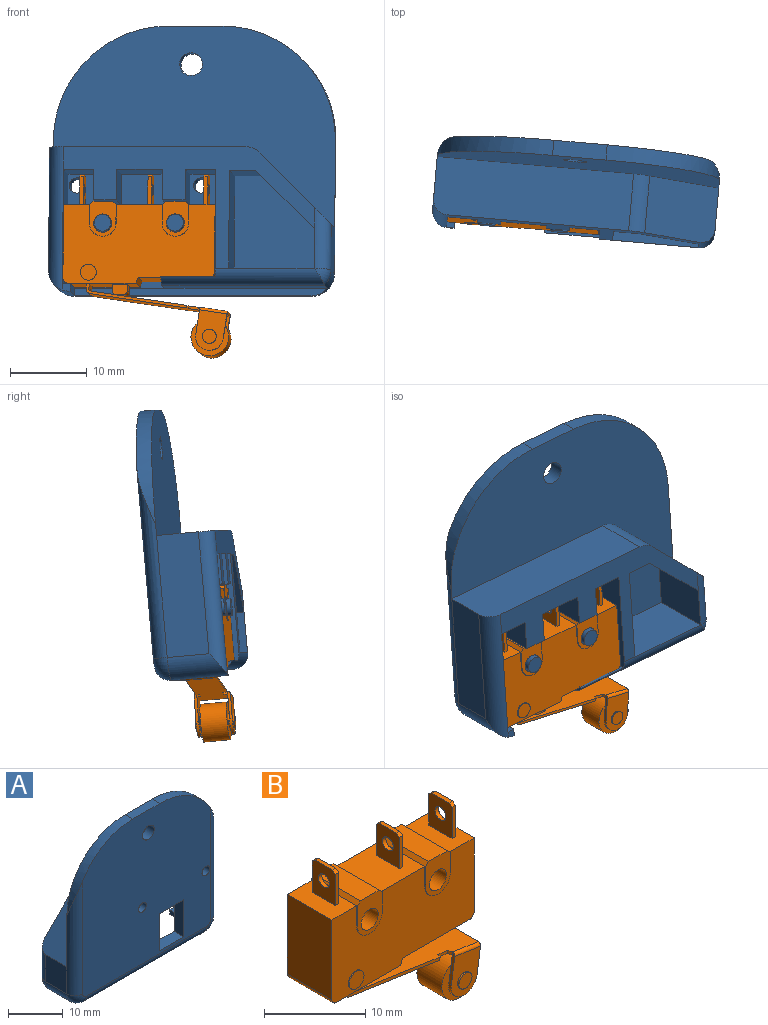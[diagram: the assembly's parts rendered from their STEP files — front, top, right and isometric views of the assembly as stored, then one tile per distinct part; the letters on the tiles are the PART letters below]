
ASSEMBLY  parts=2 mates=1
PART A: 60 faces, bbox 37x9.5x35.5 mm
  f0: plane 20x15mm, normal (0,1,0), area 203.7mm2, adj f4,f7,f8,f13,f14,f15,f16,f18
  f1: plane 33.46x33mm, normal (0,-1,0), area 982.1mm2, adj f29,f30,f31,f32,f36,f37,f40,f41
  f2: plane 33x16mm, normal (0,1,0), area 145mm2, adj f7,f8,f10,f11,f12,f13,f14,f20
  f3: plane 6x5.5mm, normal (-1,0,0), area 33mm2, adj f11,f39,f43,f46
  f4: plane 12.87x7mm, normal (0,0,1), area 12.9mm2, adj f0,f5,f15,f26,f27,f34
  f5: plane 1x1mm, normal (0,1,0), area 0.9mm2, adj f4,f27,f38,f48
  f6: plane 31x1mm, normal (0,0,-1), area 31mm2, adj f26,f38,f39,f42
  f7: plane 7x6mm, normal (0,0,-1), area 42mm2, adj f0,f2,f20,f23
  f8: plane 7x4mm, normal (0,0,-1), area 28mm2, adj f0,f2,f15,f24
  f9: plane 16x5.5mm, normal (1,0,0), area 88mm2, adj f10,f38,f40,f48
  f10: plane 25.76x7.5mm, normal (0,0,1), area 192.3mm2, adj f2,f9,f12,f28,f48
  f11: plane 9.12x9.12mm, normal (-0.71,0,0.71), area 95.5mm2, adj f2,f3,f12,f28,f46
  f12: cylinder r=3mm len=7.5mm, axis (0,1,0), area 17.7mm2, adj f2,f10,f11,f28
  f13: plane 14.01x7mm, normal (1,0,0), area 98mm2, adj f0,f2,f14,f33,f45
  f14: plane 7x4mm, normal (0,0,-1), area 28mm2, adj f0,f2,f13,f21
  f15: plane 15x7mm, normal (-1,0,0), area 105mm2, adj f0,f4,f8,f48
  f16: cylinder r=1.1mm len=7mm, axis (0,-1,0), area 48.4mm2, adj f0,f17
  f17: plane 2.2x2.2mm, normal (0,1,0), area 3.8mm2, adj f16
  f18: cylinder r=1.1mm len=7mm, axis (0,-1,0), area 48.4mm2, adj f0,f19
  f19: plane 2.2x2.2mm, normal (0,1,0), area 3.8mm2, adj f18
  f20: plane 7x4mm, normal (1,0,0), area 28mm2, adj f0,f2,f7,f22
  f21: plane 7x4mm, normal (-1,0,0), area 28mm2, adj f0,f2,f14,f22
  f22: plane 7x3mm, normal (0,0,-1), area 21mm2, adj f0,f2,f20,f21
  f23: plane 7x4mm, normal (-1,0,0), area 28mm2, adj f0,f2,f7,f25
  f24: plane 7x4mm, normal (1,0,0), area 28mm2, adj f0,f2,f8,f25
  f25: plane 7x3mm, normal (0,0,-1), area 21mm2, adj f0,f2,f23,f24
  f26: plane 33.24x1mm, normal (0,1,0), area 32.5mm2, adj f4,f6,f27,f35,f39
  f27: plane 6.5x1mm, normal (-1,0,0), area 6.5mm2, adj f4,f5,f26,f38
  f28: plane 37x26.46mm, normal (0,1,0), area 555.4mm2, adj f10,f11,f12,f29,f30,f36,f37,f40
  f29: plane 7x2mm, normal (0,0,1), area 14mm2, adj f1,f28,f36,f37
  f30: cylinder r=1.5mm len=3mm, axis (0,1,0), area 18.8mm2, adj f1,f28
  f31: cylinder r=1mm len=2.5mm, axis (0,1,0), area 15.7mm2, adj f0,f1
  f32: cylinder r=1mm len=2.5mm, axis (0,1,0), area 15.7mm2, adj f0,f1
  f33: plane 7.13x6.72mm, normal (0,0,1), area 47.9mm2, adj f0,f13,f34,f45
  f34: plane 6.72x0.99mm, normal (1,0,0), area 6.1mm2, adj f0,f4,f33,f35,f45
  f35: plane 21.37x4.5mm, normal (0,0,-1), area 96.1mm2, adj f26,f34,f39,f45
  f36: cylinder r=15mm len=15mm, axis (0,1,0), area 41mm2, adj f1,f28,f29,f43
  f37: cylinder r=15mm len=15mm, axis (0,-1,0), area 41mm2, adj f1,f28,f29,f40
  f38: cylinder r=3mm len=7.5mm, axis (0,-1,0), area 32.6mm2, adj f5,f6,f9,f27,f41,f48
  f39: cylinder r=3mm len=5.5mm, axis (0,1,0), area 14.6mm2, adj f3,f6,f26,f35,f44,f47
  f40: cylinder r=2mm len=24.94mm, axis (0,0,-1), area 67.4mm2, adj f1,f9,f28,f37,f41
  f41: torus R=1mm, axis (0,-1,0), area 11.2mm2, adj f1,f38,f40,f42
  f42: cylinder r=2mm len=31mm, axis (-1,0,0), area 97.4mm2, adj f1,f6,f41,f44
  f43: cylinder r=2mm len=24.94mm, axis (0,0,1), area 67.4mm2, adj f1,f3,f28,f36,f44
  f44: torus R=1mm, axis (0,-1,0), area 11.2mm2, adj f1,f39,f42,f43
  f45: cylinder r=2mm len=21.37mm, axis (-1,0,0), area 58.3mm2, adj f2,f13,f33,f34,f35,f47,f57
  f46: cylinder r=2mm len=8mm, axis (0,0,-1), area 21.1mm2, adj f2,f3,f11,f47,f58
  f47: torus R=1mm, axis (0,-1,0), area 4.3mm2, adj f39,f45,f46
  f48: cylinder r=2mm len=18.83mm, axis (0,0,1), area 55.5mm2, adj f2,f5,f9,f10,f15,f38
  f49: plane 6.22x2.5mm, normal (0,0,1), area 15.6mm2, adj f0,f1,f50,f52
  f50: plane 8.25x2.5mm, normal (1,0,0), area 20.6mm2, adj f0,f1,f49,f51
  f51: plane 6.22x2.5mm, normal (0,0,-1), area 15.6mm2, adj f0,f1,f50,f52
  f52: plane 8.25x2.5mm, normal (-1,0,0), area 20.6mm2, adj f0,f1,f49,f51
  f53: plane 8x7.79mm, normal (0.7,0,-0.72), area 87mm2, adj f2,f54,f58,f59
  f54: plane 8x3.43mm, normal (0,0,-1), area 27.4mm2, adj f2,f53,f55,f59
  f55: plane 11.89x8mm, normal (-1,0,0), area 95.1mm2, adj f2,f54,f56,f59
  f56: plane 8x0.98mm, normal (-1,0,-0.04), area 7.8mm2, adj f2,f55,f57,f59
  f57: plane 11.25x8mm, normal (0,0,1), area 90mm2, adj f45,f56,f58,f59
  f58: plane 8x5.28mm, normal (1,0,0), area 42.2mm2, adj f46,f53,f57,f59
  f59: plane 12.86x11.25mm, normal (0,1,0), area 114.8mm2, adj f53,f54,f55,f56,f57,f58
PART B: 105 faces, bbox 21.7x6.4x23.8 mm
  f0: cylinder r=2.48mm len=4.95mm, axis (0,-1,0), area 54.1mm2, adj f95,f96
  f1: cylinder r=0.91mm len=1.83mm, axis (0,1,0), area 1.7mm2, adj f17,f95
  f2: cylinder r=0.91mm len=1.83mm, axis (0,-1,0), area 1mm2, adj f20,f94
  f3: cylinder r=0.91mm len=1.83mm, axis (0,1,0), area 1mm2, adj f19,f93
  f4: cylinder r=1.82mm len=3.61mm, axis (0,-1,0), area 2mm2, adj f17,f20,f21,f22
  f5: cylinder r=1.82mm len=3.61mm, axis (0,-1,0), area 2mm2, adj f18,f19,f21,f92
  f6: cylinder r=0.76mm len=1.52mm, axis (-1,0,0), area 2.3mm2, adj f25,f26
  f7: cylinder r=0.76mm len=1.52mm, axis (-1,0,0), area 2.3mm2, adj f29,f31
  f8: cylinder r=0.76mm len=1.52mm, axis (-1,0,0), area 2.3mm2, adj f33,f35
  f9: cylinder r=1.04mm len=2.08mm, axis (0,-1,0), area 0.8mm2, adj f40,f69
  f10: cylinder r=1.04mm len=2.08mm, axis (0,-1,0), area 0.8mm2, adj f41,f68
  f11: cylinder r=1.19mm len=6.44mm, axis (0,1,0), area 48.3mm2, adj f46,f47
  f12: cylinder r=1.19mm len=6.44mm, axis (0,1,0), area 48.3mm2, adj f51,f52
  f13: cylinder r=0.91mm len=1.83mm, axis (0,1,0), area 1.7mm2, adj f18,f96
  f14: plane 17.99x4.06mm, normal (0.15,0,0.99), area 72.3mm2, adj f16,f21,f23,f87,f90,f91,f97,f98
  f15: plane 17.99x4.06mm, normal (-0.15,0,-0.99), area 72.3mm2, adj f16,f17,f18,f21,f23,f88,f97,f98
  f16: plane 13.23x3.18mm, normal (0,1,0), area 5mm2, adj f14,f15,f24,f86,f87,f88,f89,f102
  f17: plane 5.31x4.09mm, normal (0,-1,0), area 14.4mm2, adj f1,f4,f15,f21,f22
  f18: plane 5.31x4.09mm, normal (0,1,0), area 14.4mm2, adj f5,f13,f15,f21,f92
  f19: plane 5.31x4.09mm, normal (0,-1,0), area 14.4mm2, adj f3,f5,f21,f91,f92
  f20: plane 5.31x4.09mm, normal (0,1,0), area 14.4mm2, adj f2,f4,f21,f22,f90
  f21: plane 4.78x3.58mm, normal (0.99,0,-0.15), area 4mm2, adj f4,f5,f14,f15,f17,f18,f19,f20
  f22: plane 3.58x0.53mm, normal (-0.99,0,0.15), area 1.3mm2, adj f4,f17,f20,f90,f100
  f23: plane 13.23x3.18mm, normal (0,-1,0), area 5mm2, adj f14,f15,f24,f86,f87,f88,f89,f97
  f24: plane 8.97x6.2mm, normal (0,0,-1), area 47.8mm2, adj f16,f23,f40,f41,f57,f79,f83,f84
  f25: plane 4.09x3.24mm, normal (1,0,0), area 11.3mm2, adj f6,f27,f28,f39,f70,f75,f78
  f26: plane 4.09x3.24mm, normal (-1,0,0), area 11.3mm2, adj f6,f27,f28,f39,f70,f75,f78
  f27: plane 3.79x0.48mm, normal (0,-1,0), area 1.8mm2, adj f25,f26,f39,f75
  f28: plane 2.39x0.48mm, normal (0,0,1), area 1.2mm2, adj f25,f26,f75,f78
  f29: plane 4.09x3.24mm, normal (-1,0,0), area 11.3mm2, adj f7,f30,f32,f38,f71,f74,f77
  f30: plane 3.79x0.48mm, normal (0,-1,0), area 1.8mm2, adj f29,f31,f38,f74
  f31: plane 4.09x3.24mm, normal (1,0,0), area 11.3mm2, adj f7,f30,f32,f38,f71,f74,f77
  f32: plane 2.39x0.48mm, normal (0,0,1), area 1.2mm2, adj f29,f31,f74,f77
  f33: plane 4.09x3.24mm, normal (-1,0,0), area 11.3mm2, adj f8,f34,f36,f37,f72,f73,f76
  f34: plane 3.79x0.48mm, normal (0,-1,0), area 1.8mm2, adj f33,f35,f37,f73
  f35: plane 4.09x3.24mm, normal (1,0,0), area 11.3mm2, adj f8,f34,f36,f37,f72,f73,f76
  f36: plane 2.39x0.48mm, normal (0,0,1), area 1.2mm2, adj f33,f35,f73,f76
  f37: plane 6.2x3.45mm, normal (0,0,1), area 19.8mm2, adj f33,f34,f35,f40,f41,f54,f67,f72
  f38: plane 6.2x6.06mm, normal (0,0,1), area 36mm2, adj f29,f30,f31,f40,f41,f64,f66,f71
  f39: plane 6.2x3.45mm, normal (0,0,1), area 19.8mm2, adj f25,f26,f27,f40,f41,f55,f65,f70
  f40: plane 19.89x10.29mm, normal (0,1,0), area 167.2mm2, adj f9,f24,f37,f38,f39,f44,f49,f54
  f41: plane 19.89x10.29mm, normal (0,-1,0), area 167.2mm2, adj f10,f24,f37,f38,f39,f42,f43,f48
  f42: plane 2.43x0.12mm, normal (1,0,0), area 0.3mm2, adj f41,f46,f60,f67
  f43: plane 2.43x0.12mm, normal (-1,0,0), area 0.3mm2, adj f41,f46,f60,f66
  f44: plane 2.43x0.12mm, normal (-1,0,0), area 0.3mm2, adj f40,f47,f58,f66
  f45: plane 6.44x2.6mm, normal (0,0,1), area 16.8mm2, adj f46,f47,f66,f67
  f46: plane 4.6x3.47mm, normal (0,-1,0), area 10mm2, adj f11,f42,f43,f45,f60,f66,f67
  f47: plane 4.6x3.47mm, normal (0,1,0), area 10mm2, adj f11,f44,f45,f58,f59,f66,f67
  f48: plane 2.43x0.12mm, normal (-1,0,0), area 0.3mm2, adj f41,f51,f63,f65
  f49: plane 2.43x0.12mm, normal (-1,0,0), area 0.3mm2, adj f40,f52,f62,f65
  f50: plane 6.44x2.6mm, normal (0,0,1), area 16.8mm2, adj f51,f52,f64,f65
  f51: plane 4.6x3.47mm, normal (0,-1,0), area 10mm2, adj f12,f48,f50,f53,f63,f64,f65
  f52: plane 4.6x3.47mm, normal (0,1,0), area 10mm2, adj f12,f49,f50,f61,f62,f64,f65
  f53: plane 2.43x0.12mm, normal (1,0,0), area 0.3mm2, adj f41,f51,f63,f64
  f54: plane 8.92x6.2mm, normal (1,0,0), area 55.3mm2, adj f37,f40,f41,f104
  f55: plane 9.65x6.2mm, normal (-1,0,0), area 59.8mm2, adj f39,f40,f41,f103
  f56: plane 9.4x6.2mm, normal (0,0,-1), area 58.2mm2, adj f40,f41,f57,f104
  f57: plane 6.2x0.74mm, normal (0.95,0,-0.33), area 4.8mm2, adj f24,f40,f41,f56
  f58: cylinder r=1.73mm len=3.47mm, axis (0,1,0), area 0.7mm2, adj f40,f44,f47,f59
  f59: plane 2.43x0.12mm, normal (1,0,0), area 0.3mm2, adj f40,f47,f58,f67
  f60: cylinder r=1.73mm len=3.47mm, axis (0,1,0), area 0.7mm2, adj f41,f42,f43,f46
  f61: plane 2.43x0.12mm, normal (1,0,0), area 0.3mm2, adj f40,f52,f62,f64
  f62: cylinder r=1.73mm len=3.47mm, axis (0,1,0), area 0.7mm2, adj f40,f49,f52,f61
  f63: cylinder r=1.73mm len=3.47mm, axis (0,1,0), area 0.7mm2, adj f41,f48,f51,f53
  f64: plane 6.44x0.43mm, normal (0.71,0,0.71), area 3.9mm2, adj f38,f50,f51,f52,f53,f61
  f65: plane 6.44x0.43mm, normal (-0.71,0,0.71), area 3.9mm2, adj f39,f48,f49,f50,f51,f52
  f66: plane 6.44x0.43mm, normal (-0.71,0,0.71), area 3.9mm2, adj f38,f43,f44,f45,f46,f47
  f67: plane 6.44x0.43mm, normal (0.71,0,0.71), area 3.9mm2, adj f37,f42,f45,f46,f47,f59
  f68: plane 2.08x2.08mm, normal (0,-1,0), area 3.4mm2, adj f10
  f69: plane 2.08x2.08mm, normal (0,1,0), area 3.4mm2, adj f9
  f70: plane 3.79x0.48mm, normal (0,1,0), area 1.8mm2, adj f25,f26,f39,f78
  f71: plane 3.79x0.48mm, normal (0,1,0), area 1.8mm2, adj f29,f31,f38,f77
  f72: plane 3.79x0.48mm, normal (0,1,0), area 1.8mm2, adj f33,f35,f37,f76
  f73: plane 0.48x0.43mm, normal (0,-0.57,0.82), area 0.3mm2, adj f33,f34,f35,f36
  f74: plane 0.48x0.43mm, normal (0,-0.57,0.82), area 0.3mm2, adj f29,f30,f31,f32
  f75: plane 0.48x0.43mm, normal (0,-0.57,0.82), area 0.3mm2, adj f25,f26,f27,f28
  f76: plane 0.48x0.43mm, normal (0,0.57,0.82), area 0.3mm2, adj f33,f35,f36,f72
  f77: plane 0.48x0.43mm, normal (0,0.57,0.82), area 0.3mm2, adj f29,f31,f32,f71
  f78: plane 0.48x0.43mm, normal (0,0.57,0.82), area 0.3mm2, adj f25,f26,f28,f70
  f79: plane 3.21x0.88mm, normal (1,0,0), area 2.8mm2, adj f24,f80,f84,f85
  f80: cylinder r=0.51mm len=3.21mm, axis (0,-1,0), area 2.6mm2, adj f79,f81,f84,f85
  f81: plane 3.21x0.95mm, normal (0,0,-1), area 3.1mm2, adj f80,f82,f84,f85
  f82: cylinder r=0.51mm len=3.21mm, axis (0,-1,0), area 2.6mm2, adj f81,f83,f84,f85
  f83: plane 3.21x0.88mm, normal (-1,0,0), area 2.8mm2, adj f24,f82,f84,f85
  f84: plane 1.97x1.38mm, normal (0,1,0), area 2.6mm2, adj f24,f79,f80,f81,f82,f83
  f85: plane 1.97x1.38mm, normal (0,-1,0), area 2.6mm2, adj f24,f79,f80,f81,f82,f83
  f86: plane 4.06x0.63mm, normal (0.99,0,-0.15), area 2.6mm2, adj f16,f23,f24,f87
  f87: cylinder r=0.28mm len=4.06mm, axis (0,-1,0), area 1.8mm2, adj f14,f16,f23,f86
  f88: cylinder r=0.64mm len=4.06mm, axis (0,-1,0), area 4.1mm2, adj f15,f16,f23,f89
  f89: plane 4.06x0.58mm, normal (-0.99,0,0.15), area 2.4mm2, adj f16,f23,f24,f88
  f90: cylinder r=0.36mm len=3.65mm, axis (0.99,0,-0.15), area 2mm2, adj f14,f20,f21,f22
  f91: cylinder r=0.36mm len=3.65mm, axis (0.99,0,-0.15), area 2mm2, adj f14,f19,f21,f92
  f92: plane 3.58x0.53mm, normal (-0.99,0,0.15), area 1.3mm2, adj f5,f18,f19,f91,f99
  f93: plane 1.83x1.83mm, normal (0,-1,0), area 2.6mm2, adj f3
  f94: plane 1.83x1.83mm, normal (0,1,0), area 2.6mm2, adj f2
  f95: plane 4.95x4.95mm, normal (0,1,0), area 16.6mm2, adj f0,f1
  f96: plane 4.95x4.95mm, normal (0,-1,0), area 16.6mm2, adj f0,f13
  f97: plane 0.51x0.38mm, normal (0.93,-0.34,-0.14), area 0.2mm2, adj f14,f15,f23,f98
  f98: plane 1.45x0.56mm, normal (0,-1,0), area 0.5mm2, adj f14,f15,f97,f99
  f99: plane 0.51x0.38mm, normal (-0.93,-0.34,0.14), area 0.2mm2, adj f14,f15,f92,f98
  f100: plane 0.51x0.38mm, normal (-0.93,0.34,0.14), area 0.2mm2, adj f14,f15,f22,f101
  f101: plane 1.45x0.56mm, normal (0,1,0), area 0.5mm2, adj f14,f15,f100,f102
  f102: plane 0.51x0.38mm, normal (0.93,0.34,-0.14), area 0.2mm2, adj f14,f15,f16,f101
  f103: cylinder r=0.64mm len=6.2mm, axis (0,-1,0), area 6.2mm2, adj f24,f40,f41,f55
  f104: cylinder r=0.64mm len=6.2mm, axis (0,1,0), area 6.2mm2, adj f40,f41,f54,f56
PLACE A rot(axis=(0,0.04,1),175deg) t=(-22.84,-16.36,-7.41)mm
PLACE B rot(axis=(-0.71,0.03,-0.71),7.1deg) t=(-29.07,-12.32,-10.94)mm
MATE slider A.f18 <-> B.f11  axis (0.09,0.99,-0.09) through (-24.63,-16.25,-7.91)mm
